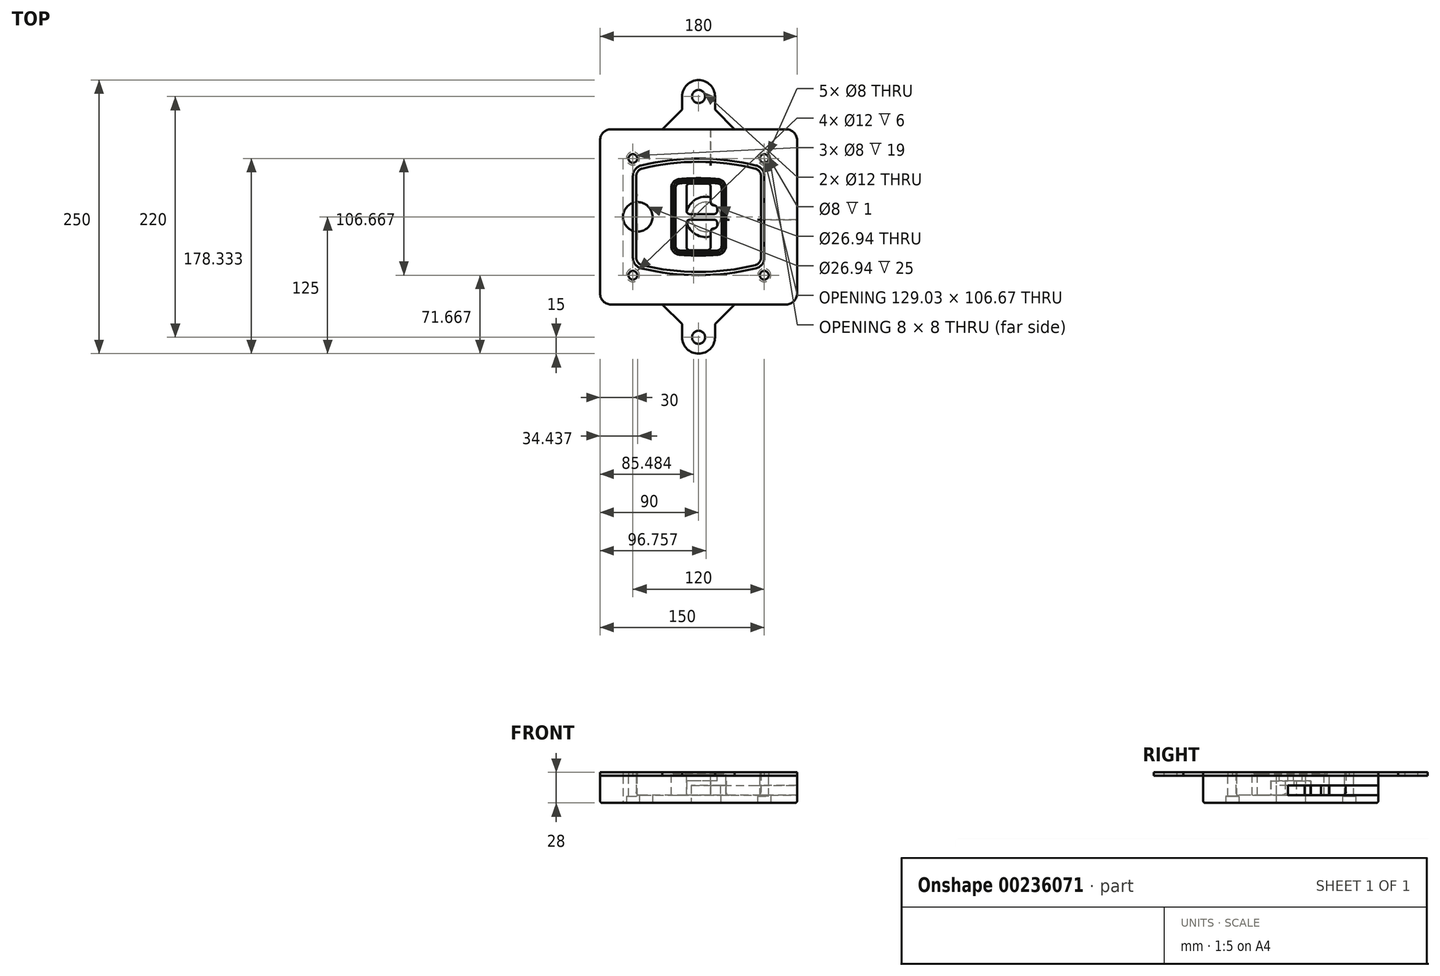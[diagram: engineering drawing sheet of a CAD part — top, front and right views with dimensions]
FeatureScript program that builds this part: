
annotation { "Feature Type Name" : "Feature", "Feature Type Description" : "" }
export const myFeature = defineFeature(function(context is Context, id is Id, definition is map)
    precondition{}
    {
        {
            var Q0;
            Q0=qCreatedBy(makeId("Top.planeOp"),FACE);
            var sketch = newSketch(context, id + "F0", { "sketchPlane" : qUnion([Q0])});
            skPoint(sketch, "E0.rect.middle", {"position": v(0, 0) * mm});
            skLineSegment(sketch, "E1.bottom", {"start": v(-80, -80) * mm, "end": v(80, -80) * mm});
            skLineSegment(sketch, "E1.top", {"start": v(-80, 80) * mm, "end": v(80, 80) * mm});
            skLineSegment(sketch, "E1.left", {"start": v(-90, -70) * mm, "end": v(-90, 70) * mm});
            skLineSegment(sketch, "E1.right", {"start": v(90, -70) * mm, "end": v(90, 70) * mm});
            skLineSegment(sketch, "E2", {"start": v(-90, 80) * mm, "end": v(90, -80) * mm, "construction": true});
            skLineSegment(sketch, "E3", {"start": v(90, 80) * mm, "end": v(-90, -80) * mm, "construction": true});
            skCircle(sketch, "E4", {"center": v(-60, 53.33) * mm, "radius": 4 * mm});
            skCircle(sketch, "E5", {"center": v(60, 53.33) * mm, "radius": 4 * mm});
            skCircle(sketch, "E6", {"center": v(60, -53.33) * mm, "radius": 4 * mm});
            skCircle(sketch, "E7", {"center": v(-60, -53.33) * mm, "radius": 4 * mm});
            skLineSegment(sketch, "E8", {"start": v(-60, 53.33) * mm, "end": v(60, 53.33) * mm, "construction": true});
            skLineSegment(sketch, "E9", {"start": v(60, 53.33) * mm, "end": v(60, -53.33) * mm, "construction": true});
            skLineSegment(sketch, "E10", {"start": v(60, -53.33) * mm, "end": v(-60, -53.33) * mm, "construction": true});
            skLineSegment(sketch, "E11", {"start": v(-60, -53.33) * mm, "end": v(-60, 53.33) * mm, "construction": true});
            skLineSegment(sketch, "E12", {"start": v(-60, 37.3) * mm, "end": v(-60, -37.3) * mm});
            skLineSegment(sketch, "E13", {"start": v(60, 37.3) * mm, "end": v(60, -37.3) * mm});
            skArc(sketch, "E14", {"start": v(52.38, 47.01) * mm, "mid": v(0, 53.33) * mm, "end": v(-52.38, 47.01) * mm});
            skArc(sketch, "E15", {"start": v(-52.38, -47.01) * mm, "mid": v(0, -53.33) * mm, "end": v(52.38, -47.01) * mm});
            skLineSegment(sketch, "E16", {"start": v(-60, 0) * mm, "end": v(60, 0) * mm, "construction": true});
            skPoint(sketch, "E17.visualSharp", {"position": v(-60, -45) * mm});
            skArc(sketch, "E17.filletArc", {"start": v(-60, -37.3) * mm, "mid": v(-57.87, -43.47) * mm, "end": v(-52.38, -47.01) * mm});
            skPoint(sketch, "E18.visualSharp", {"position": v(-60, 45) * mm});
            skArc(sketch, "E18.filletArc", {"start": v(-52.38, 47.01) * mm, "mid": v(-57.87, 43.47) * mm, "end": v(-60, 37.3) * mm});
            skPoint(sketch, "E19.visualSharp", {"position": v(60, 45) * mm});
            skArc(sketch, "E19.filletArc", {"start": v(60, 37.3) * mm, "mid": v(57.87, 43.47) * mm, "end": v(52.38, 47.01) * mm});
            skPoint(sketch, "E20.visualSharp", {"position": v(60, -45) * mm});
            skArc(sketch, "E20.filletArc", {"start": v(52.38, -47.01) * mm, "mid": v(57.87, -43.47) * mm, "end": v(60, -37.3) * mm});
            skPoint(sketch, "E21.visualSharp", {"position": v(-90, 80) * mm});
            skArc(sketch, "E21.filletArc", {"start": v(-80, 80) * mm, "mid": v(-87.07, 77.07) * mm, "end": v(-90, 70) * mm});
            skPoint(sketch, "E22.visualSharp", {"position": v(90, 80) * mm});
            skArc(sketch, "E22.filletArc", {"start": v(90, 70) * mm, "mid": v(87.07, 77.07) * mm, "end": v(80, 80) * mm});
            skPoint(sketch, "E23.visualSharp", {"position": v(90, -80) * mm});
            skArc(sketch, "E23.filletArc", {"start": v(80, -80) * mm, "mid": v(87.07, -77.07) * mm, "end": v(90, -70) * mm});
            skPoint(sketch, "E24.visualSharp", {"position": v(-90, -80) * mm});
            skArc(sketch, "E24.filletArc", {"start": v(-90, -70) * mm, "mid": v(-87.07, -77.07) * mm, "end": v(-80, -80) * mm});
            skArc(sketch, "E25.0", {"start": v(57, 37.3) * mm, "mid": v(55.5, 41.62) * mm, "end": v(51.67, 44.1) * mm});
            skLineSegment(sketch, "E25.1", {"start": v(57, 37.3) * mm, "end": v(57, -37.3) * mm});
            skArc(sketch, "E25.2", {"start": v(51.67, -44.1) * mm, "mid": v(55.5, -41.62) * mm, "end": v(57, -37.3) * mm});
            skArc(sketch, "E25.3", {"start": v(-51.67, -44.1) * mm, "mid": v(0, -50.33) * mm, "end": v(51.67, -44.1) * mm});
            skArc(sketch, "E25.4", {"start": v(-57, -37.3) * mm, "mid": v(-55.5, -41.62) * mm, "end": v(-51.67, -44.1) * mm});
            skArc(sketch, "E25.5", {"start": v(51.67, 44.1) * mm, "mid": v(0, 50.33) * mm, "end": v(-51.67, 44.1) * mm});
            skLineSegment(sketch, "E25.6", {"start": v(-57, 37.3) * mm, "end": v(-57, -37.3) * mm});
            skArc(sketch, "E25.7", {"start": v(-51.67, 44.1) * mm, "mid": v(-55.5, 41.62) * mm, "end": v(-57, 37.3) * mm});
            skArc(sketch, "E26.0", {"start": v(-53.33, 50.9) * mm, "mid": v(-61.01, 45.94) * mm, "end": v(-64, 37.3) * mm});
            skArc(sketch, "E26.1", {"start": v(53.33, 50.9) * mm, "mid": v(0, 57.33) * mm, "end": v(-53.33, 50.9) * mm});
            skArc(sketch, "E26.2", {"start": v(64, 37.3) * mm, "mid": v(61.01, 45.94) * mm, "end": v(53.33, 50.9) * mm});
            skLineSegment(sketch, "E26.3", {"start": v(64, 37.3) * mm, "end": v(64, -37.3) * mm});
            skArc(sketch, "E26.4", {"start": v(53.33, -50.9) * mm, "mid": v(61.01, -45.94) * mm, "end": v(64, -37.3) * mm});
            skLineSegment(sketch, "E26.5", {"start": v(-64, 37.3) * mm, "end": v(-64, -37.3) * mm});
            skArc(sketch, "E26.6", {"start": v(-53.33, -50.9) * mm, "mid": v(0, -57.33) * mm, "end": v(53.33, -50.9) * mm});
            skArc(sketch, "E26.7", {"start": v(-64, -37.3) * mm, "mid": v(-61.01, -45.94) * mm, "end": v(-53.33, -50.9) * mm});
            skSolve(sketch);
        }
        {
            var Q0;
            Q0=makeQuery(id+"F0.imprint","IMPRINT",FACE,{"disambiguationData":[TD([[makeQuery(id+"F0.imprint","IMPRINT",EDGE,{"derivedFrom":sQuery(id+"F0.wireOp",EDGE,"E1.bottom")}),1.0]])]});
            var Q1;
            Q1=makeQuery(id+"F0.imprint","IMPRINT",FACE,{"disambiguationData":[TD([[makeQuery(id+"F0.imprint","IMPRINT",EDGE,{"derivedFrom":sQuery(id+"F0.wireOp",EDGE,"E12")}),1.0]])]});
            var Q2;
            Q2=makeQuery(id+"F0.imprint","IMPRINT",FACE,{"disambiguationData":[TD([[makeQuery(id+"F0.imprint","IMPRINT",EDGE,{"derivedFrom":sQuery(id+"F0.wireOp",EDGE,"E25.0")}),1.0]])]});
            var Q3;
            Q3=makeQuery(id+"F0.imprint","IMPRINT",FACE,{"disambiguationData":[TD([[makeQuery(id+"F0.imprint","IMPRINT",EDGE,{"derivedFrom":sQuery(id+"F0.wireOp",EDGE,"E12")}),-1.0]])]});
            extrude(context, id + "F1", {"entities" : qUnion([Q0, Q1, Q2, Q3]), "oppositeDirection" : true, "depth" : 25 * mm});
        }
        {
            var Q0;
            Q0=makeQuery(id+"F0.imprint","IMPRINT",FACE,{"disambiguationData":[TD([[makeQuery(id+"F0.imprint","IMPRINT",EDGE,{"derivedFrom":sQuery(id+"F0.wireOp",EDGE,"E12")}),1.0]])]});
            extrude(context, id + "F2", {"entities" : qUnion([Q0]), "operationType" : NewBodyOperationType.ADD, "depth" : 3 * mm});
        }
        {
            var Q0;
            Q0=makeQuery(id+"F0.imprint","IMPRINT",FACE,{"disambiguationData":[TD([[makeQuery(id+"F0.imprint","IMPRINT",EDGE,{"derivedFrom":sQuery(id+"F0.wireOp",EDGE,"E25.0")}),1.0]])]});
            extrude(context, id + "F3", {"entities" : qUnion([Q0]), "operationType" : NewBodyOperationType.REMOVE, "oppositeDirection" : true, "depth" : 18 * mm});
        }
        {
            var Q0;
            Q0=makeQuery(id+"F2.opExtrude","CAP_FACE",FACE,{"disambiguationData":[OSD([sQuery(id+"F0.wireOp",EDGE,"E12"),sQuery(id+"F0.wireOp",EDGE,"E13"),sQuery(id+"F0.wireOp",EDGE,"E14"),sQuery(id+"F0.wireOp",EDGE,"E15"),sQuery(id+"F0.wireOp",EDGE,"E17.filletArc"),sQuery(id+"F0.wireOp",EDGE,"E18.filletArc"),sQuery(id+"F0.wireOp",EDGE,"E19.filletArc"),sQuery(id+"F0.wireOp",EDGE,"E20.filletArc"),sQuery(id+"F0.wireOp",EDGE,"E25.0"),sQuery(id+"F0.wireOp",EDGE,"E25.1"),sQuery(id+"F0.wireOp",EDGE,"E25.2"),sQuery(id+"F0.wireOp",EDGE,"E25.3"),sQuery(id+"F0.wireOp",EDGE,"E25.4"),sQuery(id+"F0.wireOp",EDGE,"E25.5"),sQuery(id+"F0.wireOp",EDGE,"E25.6"),sQuery(id+"F0.wireOp",EDGE,"E25.7")])],"isStart":false});
            var sketch = newSketch(context, id + "F4", { "sketchPlane" : qUnion([Q0])});
            skArc(sketch, "E27.0", {"start": v(-17.7, -34.56) * mm, "mid": v(0, -35.33) * mm, "end": v(17.7, -34.56) * mm});
            skArc(sketch, "E28.0", {"start": v(17.7, 34.56) * mm, "mid": v(0, 35.33) * mm, "end": v(-17.7, 34.56) * mm});
            skLineSegment(sketch, "E29", {"start": v(-25, 26.59) * mm, "end": v(-25, -26.59) * mm});
            skLineSegment(sketch, "E30", {"start": v(25, 26.59) * mm, "end": v(25, -26.59) * mm});
            skLineSegment(sketch, "E31", {"start": v(-25, 33.78) * mm, "end": v(25, 33.78) * mm, "construction": true});
            skLineSegment(sketch, "E32", {"start": v(-25, -33.78) * mm, "end": v(25, -33.78) * mm, "construction": true});
            skPoint(sketch, "E33.visualSharp", {"position": v(-25, 33.78) * mm});
            skArc(sketch, "E33.filletArc", {"start": v(-17.7, 34.56) * mm, "mid": v(-22.9, 32) * mm, "end": v(-25, 26.59) * mm});
            skPoint(sketch, "E34.visualSharp", {"position": v(25, 33.78) * mm});
            skArc(sketch, "E34.filletArc", {"start": v(25, 26.59) * mm, "mid": v(22.9, 32) * mm, "end": v(17.7, 34.56) * mm});
            skPoint(sketch, "E35.visualSharp", {"position": v(25, -33.78) * mm});
            skArc(sketch, "E35.filletArc", {"start": v(17.7, -34.56) * mm, "mid": v(22.9, -32) * mm, "end": v(25, -26.59) * mm});
            skPoint(sketch, "E36.visualSharp", {"position": v(-25, -33.78) * mm});
            skArc(sketch, "E36.filletArc", {"start": v(-25, -26.59) * mm, "mid": v(-22.9, -32) * mm, "end": v(-17.7, -34.56) * mm});
            skArc(sketch, "E37.0", {"start": v(51.67, 44.1) * mm, "mid": v(0, 50.33) * mm, "end": v(-51.67, 44.1) * mm});
            skArc(sketch, "E37.1", {"start": v(-51.67, 44.1) * mm, "mid": v(-55.5, 41.62) * mm, "end": v(-57, 37.3) * mm});
            skLineSegment(sketch, "E37.2", {"start": v(-57, 37.3) * mm, "end": v(-57, -37.3) * mm});
            skArc(sketch, "E37.3", {"start": v(-57, -37.3) * mm, "mid": v(-55.5, -41.62) * mm, "end": v(-51.67, -44.1) * mm});
            skArc(sketch, "E37.4", {"start": v(-51.67, -44.1) * mm, "mid": v(0, -50.33) * mm, "end": v(51.67, -44.1) * mm});
            skArc(sketch, "E37.5", {"start": v(51.67, -44.1) * mm, "mid": v(55.5, -41.62) * mm, "end": v(57, -37.3) * mm});
            skLineSegment(sketch, "E37.6", {"start": v(57, 37.3) * mm, "end": v(57, -37.3) * mm});
            skArc(sketch, "E37.7", {"start": v(57, 37.3) * mm, "mid": v(55.5, 41.62) * mm, "end": v(51.67, 44.1) * mm});
            skLineSegment(sketch, "E38.0", {"start": v(23, 26.59) * mm, "end": v(23, -26.59) * mm});
            skArc(sketch, "E38.1", {"start": v(17.53, -32.56) * mm, "mid": v(21.42, -30.64) * mm, "end": v(23, -26.59) * mm});
            skArc(sketch, "E38.2", {"start": v(-17.53, -32.56) * mm, "mid": v(0, -33.33) * mm, "end": v(17.53, -32.56) * mm});
            skArc(sketch, "E38.3", {"start": v(-23, -26.59) * mm, "mid": v(-21.42, -30.64) * mm, "end": v(-17.53, -32.56) * mm});
            skLineSegment(sketch, "E38.4", {"start": v(-23, 26.59) * mm, "end": v(-23, -26.59) * mm});
            skArc(sketch, "E38.5", {"start": v(23, 26.59) * mm, "mid": v(21.42, 30.64) * mm, "end": v(17.53, 32.56) * mm});
            skArc(sketch, "E38.6", {"start": v(-17.53, 32.56) * mm, "mid": v(-21.42, 30.64) * mm, "end": v(-23, 26.59) * mm});
            skArc(sketch, "E38.7", {"start": v(17.53, 32.56) * mm, "mid": v(0, 33.33) * mm, "end": v(-17.53, 32.56) * mm});
            skArc(sketch, "E39.0", {"start": v(21, 26.59) * mm, "mid": v(19.95, 29.29) * mm, "end": v(17.35, 30.57) * mm});
            skLineSegment(sketch, "E39.1", {"start": v(21, 26.59) * mm, "end": v(21, -26.59) * mm});
            skArc(sketch, "E39.2", {"start": v(17.35, -30.57) * mm, "mid": v(19.95, -29.29) * mm, "end": v(21, -26.59) * mm});
            skArc(sketch, "E39.3", {"start": v(-17.35, -30.57) * mm, "mid": v(0, -31.33) * mm, "end": v(17.35, -30.57) * mm});
            skArc(sketch, "E39.4", {"start": v(-21, -26.59) * mm, "mid": v(-19.95, -29.29) * mm, "end": v(-17.35, -30.57) * mm});
            skArc(sketch, "E39.5", {"start": v(17.35, 30.57) * mm, "mid": v(0, 31.33) * mm, "end": v(-17.35, 30.57) * mm});
            skLineSegment(sketch, "E39.6", {"start": v(-21, 26.59) * mm, "end": v(-21, -26.59) * mm});
            skArc(sketch, "E39.7", {"start": v(-17.35, 30.57) * mm, "mid": v(-19.95, 29.29) * mm, "end": v(-21, 26.59) * mm});
            skLineSegment(sketch, "E40", {"start": v(-25, 0) * mm, "end": v(25, 0) * mm, "construction": true});
            skLineSegment(sketch, "E41", {"start": v(-11, 5.5) * mm, "end": v(-11, 27.5) * mm});
            skLineSegment(sketch, "E42", {"start": v(-8, 30.5) * mm, "end": v(8, 30.5) * mm});
            skLineSegment(sketch, "E43", {"start": v(11, 27.5) * mm, "end": v(11, 13.5) * mm});
            skLineSegment(sketch, "E44", {"start": v(14, 10.5) * mm, "end": v(14, 10.5) * mm});
            skLineSegment(sketch, "E45", {"start": v(17, 7.5) * mm, "end": v(17, 5.5) * mm});
            skLineSegment(sketch, "E46", {"start": v(14, 2.5) * mm, "end": v(-8, 2.5) * mm});
            skPoint(sketch, "E47.visualSharp", {"position": v(-11, 30.5) * mm});
            skArc(sketch, "E47.filletArc", {"start": v(-8, 30.5) * mm, "mid": v(-10.12, 29.62) * mm, "end": v(-11, 27.5) * mm});
            skPoint(sketch, "E48.visualSharp", {"position": v(11, 30.5) * mm});
            skArc(sketch, "E48.filletArc", {"start": v(11, 27.5) * mm, "mid": v(10.12, 29.62) * mm, "end": v(8, 30.5) * mm});
            skPoint(sketch, "E49.visualSharp", {"position": v(11, 10.5) * mm});
            skArc(sketch, "E49.filletArc", {"start": v(11, 13.5) * mm, "mid": v(11.88, 11.38) * mm, "end": v(14, 10.5) * mm});
            skPoint(sketch, "E50.visualSharp", {"position": v(17, 10.5) * mm});
            skArc(sketch, "E50.filletArc", {"start": v(17, 7.5) * mm, "mid": v(16.12, 9.62) * mm, "end": v(14, 10.5) * mm});
            skPoint(sketch, "E51.visualSharp", {"position": v(17, 2.5) * mm});
            skArc(sketch, "E51.filletArc", {"start": v(14, 2.5) * mm, "mid": v(16.12, 3.38) * mm, "end": v(17, 5.5) * mm});
            skPoint(sketch, "E52.visualSharp", {"position": v(-11, 2.5) * mm});
            skArc(sketch, "E52.filletArc", {"start": v(-11, 5.5) * mm, "mid": v(-10.12, 3.38) * mm, "end": v(-8, 2.5) * mm});
            skLineSegment(sketch, "E53.0.MirrorCS", {"start": v(14, -2.5) * mm, "end": v(-8, -2.5) * mm});
            skArc(sketch, "E54.0.MirrorCS", {"start": v(-11, -5.5) * mm, "mid": v(-10.12, -3.38) * mm, "end": v(-8, -2.5) * mm});
            skLineSegment(sketch, "E55.0.MirrorCS", {"start": v(-11, -5.5) * mm, "end": v(-11, -27.5) * mm});
            skArc(sketch, "E56.0.MirrorCS", {"start": v(-8, -30.5) * mm, "mid": v(-10.12, -29.62) * mm, "end": v(-11, -27.5) * mm});
            skLineSegment(sketch, "E57.0.MirrorCS", {"start": v(-8, -30.5) * mm, "end": v(8, -30.5) * mm});
            skArc(sketch, "E58.0.MirrorCS", {"start": v(11, -27.5) * mm, "mid": v(10.12, -29.62) * mm, "end": v(8, -30.5) * mm});
            skLineSegment(sketch, "E59.0.MirrorCS", {"start": v(11, -27.5) * mm, "end": v(11, -13.5) * mm});
            skArc(sketch, "E60.0.MirrorCS", {"start": v(11, -13.5) * mm, "mid": v(11.88, -11.38) * mm, "end": v(14, -10.5) * mm});
            skArc(sketch, "E61.0.MirrorCS", {"start": v(17, -7.5) * mm, "mid": v(16.12, -9.62) * mm, "end": v(14, -10.5) * mm});
            skLineSegment(sketch, "E62.0.MirrorCS", {"start": v(17, -7.5) * mm, "end": v(17, -5.5) * mm});
            skArc(sketch, "E63.0.MirrorCS", {"start": v(14, -2.5) * mm, "mid": v(16.12, -3.38) * mm, "end": v(17, -5.5) * mm});
            skSolve(sketch);
        }
        {
            var Q0;
            Q0=makeQuery(id+"F4.imprint","IMPRINT",FACE,{"disambiguationData":[TD([[makeQuery(id+"F4.imprint","IMPRINT",EDGE,{"derivedFrom":sQuery(id+"F4.wireOp",EDGE,"E27.0")}),1.0]])]});
            var Q1;
            Q1=makeQuery(id+"F4.imprint","IMPRINT",FACE,{"disambiguationData":[TD([[makeQuery(id+"F4.imprint","IMPRINT",EDGE,{"derivedFrom":sQuery(id+"F4.wireOp",EDGE,"E38.0")}),-1.0]])]});
            var Q2;
            Q2=makeQuery(id+"F4.imprint","IMPRINT",FACE,{"disambiguationData":[TD([[makeQuery(id+"F4.imprint","IMPRINT",EDGE,{"derivedFrom":sQuery(id+"F4.wireOp",EDGE,"E39.0")}),1.0]])]});
            extrude(context, id + "F5", {"entities" : qUnion([Q0, Q1, Q2]), "operationType" : NewBodyOperationType.ADD, "endBound" : BoundingType.UP_TO_NEXT, "oppositeDirection" : true, "depth" : 25 * mm});
        }
        {
            var Q0;
            Q0=makeQuery(id+"F4.imprint","IMPRINT",FACE,{"disambiguationData":[TD([[makeQuery(id+"F4.imprint","IMPRINT",EDGE,{"derivedFrom":sQuery(id+"F4.wireOp",EDGE,"E38.0")}),-1.0]])]});
            extrude(context, id + "F6", {"entities" : qUnion([Q0]), "operationType" : NewBodyOperationType.REMOVE, "oppositeDirection" : true, "depth" : 2 * mm});
        }
        {
            var Q0;
            Q0=makeQuery(id+"F1.opExtrude","CAP_FACE",FACE,{"disambiguationData":[OSD([sQuery(id+"F0.wireOp",EDGE,"E1.bottom"),sQuery(id+"F0.wireOp",EDGE,"E1.top"),sQuery(id+"F0.wireOp",EDGE,"E1.left"),sQuery(id+"F0.wireOp",EDGE,"E1.right"),sQuery(id+"F0.wireOp",EDGE,"E4"),sQuery(id+"F0.wireOp",EDGE,"E5"),sQuery(id+"F0.wireOp",EDGE,"E6"),sQuery(id+"F0.wireOp",EDGE,"E7"),sQuery(id+"F0.wireOp",EDGE,"E21.filletArc"),sQuery(id+"F0.wireOp",EDGE,"E22.filletArc"),sQuery(id+"F0.wireOp",EDGE,"E23.filletArc"),sQuery(id+"F0.wireOp",EDGE,"E24.filletArc")])],"isStart":false});
            var sketch = newSketch(context, id + "F7", { "sketchPlane" : qUnion([Q0])});
            skCircle(sketch, "E64", {"center": v(6.76, 0) * mm, "radius": 13.47 * mm});
            skCircle(sketch, "E65", {"center": v(-55.56, 0) * mm, "radius": 13.47 * mm});
            skLineSegment(sketch, "E66", {"start": v(90, 0) * mm, "end": v(-90, 0) * mm});
            skCircle(sketch, "E67", {"center": v(6.76, 0) * mm, "radius": 18.47 * mm});
            skCircle(sketch, "E68", {"center": v(60, -53.33) * mm, "radius": 6 * mm});
            skCircle(sketch, "E69", {"center": v(-60, -53.33) * mm, "radius": 6 * mm});
            skCircle(sketch, "E70", {"center": v(-60, 53.33) * mm, "radius": 6 * mm});
            skCircle(sketch, "E71", {"center": v(60, 53.33) * mm, "radius": 6 * mm});
            skSolve(sketch);
        }
        {
            var Q0;
            {var subQ1=sQuery(id+"F7.wireOp",EDGE,"E66");var subQ4=sQuery(id+"F7.wireOp",EDGE,"E64");var subQ6=makeQuery(id+"F7.imprint","INTERSECT",VERTEX,{"disambiguationData":[OD(0.0)],"derivedFrom":[subQ4,subQ1]});Q0=makeQuery(id+"F7.imprint","IMPRINT",FACE,{"disambiguationData":[TD([[makeQuery(id+"F7.imprint","IMPRINT",EDGE,{"disambiguationData":[TD([[subQ6,-1.0]])],"derivedFrom":subQ4}),-1.0]])]});}
            var Q1;
            {var subQ0=sQuery(id+"F7.wireOp",EDGE,"E66");var subQ1=sQuery(id+"F7.wireOp",EDGE,"E64");var subQ3=makeQuery(id+"F7.imprint","INTERSECT",VERTEX,{"disambiguationData":[OD(0.0)],"derivedFrom":[subQ1,subQ0]});Q1=makeQuery(id+"F7.imprint","IMPRINT",FACE,{"disambiguationData":[TD([[makeQuery(id+"F7.imprint","IMPRINT",EDGE,{"disambiguationData":[TD([[subQ3,-1.0]])],"derivedFrom":subQ1}),1.0]])]});}
            var Q2;
            {var subQ0=sQuery(id+"F7.wireOp",EDGE,"E66");var subQ1=sQuery(id+"F7.wireOp",EDGE,"E64");var subQ3=makeQuery(id+"F7.imprint","INTERSECT",VERTEX,{"disambiguationData":[OD(0.0)],"derivedFrom":[subQ1,subQ0]});Q2=makeQuery(id+"F7.imprint","IMPRINT",FACE,{"disambiguationData":[TD([[makeQuery(id+"F7.imprint","IMPRINT",EDGE,{"disambiguationData":[TD([[subQ3,1.0]])],"derivedFrom":subQ1}),1.0]])]});}
            var Q3;
            {var subQ1=sQuery(id+"F7.wireOp",EDGE,"E66");var subQ4=sQuery(id+"F7.wireOp",EDGE,"E64");var subQ6=makeQuery(id+"F7.imprint","INTERSECT",VERTEX,{"disambiguationData":[OD(0.0)],"derivedFrom":[subQ4,subQ1]});Q3=makeQuery(id+"F7.imprint","IMPRINT",FACE,{"disambiguationData":[TD([[makeQuery(id+"F7.imprint","IMPRINT",EDGE,{"disambiguationData":[TD([[subQ6,1.0]])],"derivedFrom":subQ4}),-1.0]])]});}
            extrude(context, id + "F8", {"entities" : qUnion([Q0, Q1, Q2, Q3]), "operationType" : NewBodyOperationType.ADD, "oppositeDirection" : true, "depth" : 20 * mm});
        }
        {
            var Q0;
            {var subQ0=sQuery(id+"F7.wireOp",EDGE,"E66");var subQ1=sQuery(id+"F7.wireOp",EDGE,"E64");var subQ3=makeQuery(id+"F7.imprint","INTERSECT",VERTEX,{"disambiguationData":[OD(0.0)],"derivedFrom":[subQ1,subQ0]});Q0=makeQuery(id+"F7.imprint","IMPRINT",FACE,{"disambiguationData":[TD([[makeQuery(id+"F7.imprint","IMPRINT",EDGE,{"disambiguationData":[TD([[subQ3,-1.0]])],"derivedFrom":subQ1}),1.0]])]});}
            var Q1;
            {var subQ0=sQuery(id+"F7.wireOp",EDGE,"E66");var subQ1=sQuery(id+"F7.wireOp",EDGE,"E64");var subQ3=makeQuery(id+"F7.imprint","INTERSECT",VERTEX,{"disambiguationData":[OD(0.0)],"derivedFrom":[subQ1,subQ0]});Q1=makeQuery(id+"F7.imprint","IMPRINT",FACE,{"disambiguationData":[TD([[makeQuery(id+"F7.imprint","IMPRINT",EDGE,{"disambiguationData":[TD([[subQ3,1.0]])],"derivedFrom":subQ1}),1.0]])]});}
            extrude(context, id + "F9", {"entities" : qUnion([Q0, Q1]), "operationType" : NewBodyOperationType.REMOVE, "oppositeDirection" : true, "depth" : 16 * mm});
        }
        {
            var Q0;
            {var subQ0=sQuery(id+"F7.wireOp",EDGE,"E66");var subQ1=sQuery(id+"F7.wireOp",EDGE,"E65");var subQ3=makeQuery(id+"F7.imprint","INTERSECT",VERTEX,{"disambiguationData":[OD(0.0)],"derivedFrom":[subQ1,subQ0]});Q0=makeQuery(id+"F7.imprint","IMPRINT",FACE,{"disambiguationData":[TD([[makeQuery(id+"F7.imprint","IMPRINT",EDGE,{"disambiguationData":[TD([[subQ3,-1.0]])],"derivedFrom":subQ1}),1.0]])]});}
            var Q1;
            {var subQ0=sQuery(id+"F7.wireOp",EDGE,"E66");var subQ1=sQuery(id+"F7.wireOp",EDGE,"E65");var subQ3=makeQuery(id+"F7.imprint","INTERSECT",VERTEX,{"disambiguationData":[OD(0.0)],"derivedFrom":[subQ1,subQ0]});Q1=makeQuery(id+"F7.imprint","IMPRINT",FACE,{"disambiguationData":[TD([[makeQuery(id+"F7.imprint","IMPRINT",EDGE,{"disambiguationData":[TD([[subQ3,1.0]])],"derivedFrom":subQ1}),1.0]])]});}
            extrude(context, id + "F10", {"entities" : qUnion([Q0, Q1]), "operationType" : NewBodyOperationType.REMOVE, "oppositeDirection" : true, "depth" : 25 * mm});
        }
        {
            var Q0;
            Q0=makeQuery(id+"F7.imprint","IMPRINT",FACE,{"disambiguationData":[TD([[makeQuery(id+"F7.imprint","IMPRINT",EDGE,{"derivedFrom":sQuery(id+"F7.wireOp",EDGE,"E68")}),1.0]])]});
            var Q1;
            Q1=makeQuery(id+"F7.imprint","IMPRINT",FACE,{"disambiguationData":[TD([[makeQuery(id+"F7.imprint","IMPRINT",EDGE,{"derivedFrom":makeQuery(id+"F1.opExtrude","CAP_EDGE",EDGE,{"disambiguationData":[OSD([sQuery(id+"F0.wireOp",EDGE,"E5")])],"isStart":false})}),-1.0]])]});
            var Q2;
            Q2=makeQuery(id+"F7.imprint","IMPRINT",FACE,{"disambiguationData":[TD([[makeQuery(id+"F7.imprint","IMPRINT",EDGE,{"derivedFrom":sQuery(id+"F7.wireOp",EDGE,"E69")}),1.0]])]});
            var Q3;
            Q3=makeQuery(id+"F7.imprint","IMPRINT",FACE,{"disambiguationData":[TD([[makeQuery(id+"F7.imprint","IMPRINT",EDGE,{"derivedFrom":makeQuery(id+"F1.opExtrude","CAP_EDGE",EDGE,{"disambiguationData":[OSD([sQuery(id+"F0.wireOp",EDGE,"E4")])],"isStart":false})}),-1.0]])]});
            var Q4;
            Q4=makeQuery(id+"F7.imprint","IMPRINT",FACE,{"disambiguationData":[TD([[makeQuery(id+"F7.imprint","IMPRINT",EDGE,{"derivedFrom":sQuery(id+"F7.wireOp",EDGE,"E70")}),1.0]])]});
            var Q5;
            Q5=makeQuery(id+"F7.imprint","IMPRINT",FACE,{"disambiguationData":[TD([[makeQuery(id+"F7.imprint","IMPRINT",EDGE,{"derivedFrom":makeQuery(id+"F1.opExtrude","CAP_EDGE",EDGE,{"disambiguationData":[OSD([sQuery(id+"F0.wireOp",EDGE,"E7")])],"isStart":false})}),-1.0]])]});
            var Q6;
            Q6=makeQuery(id+"F7.imprint","IMPRINT",FACE,{"disambiguationData":[TD([[makeQuery(id+"F7.imprint","IMPRINT",EDGE,{"derivedFrom":sQuery(id+"F7.wireOp",EDGE,"E71")}),1.0]])]});
            var Q7;
            Q7=makeQuery(id+"F7.imprint","IMPRINT",FACE,{"disambiguationData":[TD([[makeQuery(id+"F7.imprint","IMPRINT",EDGE,{"derivedFrom":makeQuery(id+"F1.opExtrude","CAP_EDGE",EDGE,{"disambiguationData":[OSD([sQuery(id+"F0.wireOp",EDGE,"E6")])],"isStart":false})}),-1.0]])]});
            extrude(context, id + "F11", {"entities" : qUnion([Q0, Q1, Q2, Q3, Q4, Q5, Q6, Q7]), "operationType" : NewBodyOperationType.REMOVE, "oppositeDirection" : true, "depth" : 6 * mm});
        }
        {
            var Q0;
            Q0=makeQuery(id+"F9.boolean.opBoolean","COPY",FACE,{"derivedFrom":makeQuery(id+"F9.opExtrude","CAP_FACE",FACE,{"disambiguationData":[OSD([sQuery(id+"F7.wireOp",EDGE,"E64")])],"isStart":false})});
            var sketch = newSketch(context, id + "F12", { "sketchPlane" : qUnion([Q0])});
            skArc(sketch, "E72.0", {"start": v(11, -88.19) * mm, "mid": v(97.1, -83.6) * mm, "end": v(92.5, 2.5) * mm});
            skLineSegment(sketch, "E72.1", {"start": v(11, -17.97) * mm, "end": v(11, -17.97) * mm});
            skLineSegment(sketch, "E73", {"start": v(92.5, -105.13) * mm, "end": v(102.3, -105.13) * mm});
            skLineSegment(sketch, "E74.0", {"start": v(92.5, 2.5) * mm, "end": v(14, 2.5) * mm});
            skArc(sketch, "E74.1", {"start": v(14, 2.5) * mm, "mid": v(16.12, 3.38) * mm, "end": v(17, 5.5) * mm});
            skLineSegment(sketch, "E74.2", {"start": v(17, 7.5) * mm, "end": v(17, 5.5) * mm});
            skArc(sketch, "E74.3", {"start": v(17, 7.5) * mm, "mid": v(16.12, 9.62) * mm, "end": v(14, 10.5) * mm});
            skArc(sketch, "E74.4", {"start": v(11, 13.5) * mm, "mid": v(11.88, 11.38) * mm, "end": v(14, 10.5) * mm});
            skLineSegment(sketch, "E74.5", {"start": v(11, 13.5) * mm, "end": v(11, -88.19) * mm});
            skLineSegment(sketch, "E74.7", {"start": v(92.5, -2.5) * mm, "end": v(14, -2.5) * mm});
            skArc(sketch, "E74.8", {"start": v(14, -2.5) * mm, "mid": v(16.12, -3.38) * mm, "end": v(17, -5.5) * mm});
            skLineSegment(sketch, "E74.9", {"start": v(17, -7.5) * mm, "end": v(17, -5.5) * mm});
            skArc(sketch, "E74.10", {"start": v(17, -7.5) * mm, "mid": v(16.12, -9.62) * mm, "end": v(14, -10.5) * mm});
            skArc(sketch, "E74.11", {"start": v(11, -13.5) * mm, "mid": v(11.88, -11.38) * mm, "end": v(14, -10.5) * mm});
            skLineSegment(sketch, "E74.12", {"start": v(11, -17.97) * mm, "end": v(11, -13.5) * mm});
            skPoint(sketch, "E75.orphan", {"position": v(11, -27.5) * mm});
            skPoint(sketch, "E76.orphan", {"position": v(-8, -2.5) * mm});
            skPoint(sketch, "E77.orphan", {"position": v(-8, 2.5) * mm});
            skPoint(sketch, "E78.orphan", {"position": v(11, 27.5) * mm});
            skSolve(sketch);
        }
        {
            var Q0;
            {var subQ7=sQuery(id+"F12.wireOp",EDGE,"E72.0");var subQ14=sQuery(id+"F12.wireOp",EDGE,"E72.1");var subQ16=sQuery(id+"F12.wireOp",EDGE,"E74.1");var subQ18=sQuery(id+"F12.wireOp",EDGE,"E74.8");Q0=qUnion([makeQuery(id+"F12.imprint","IMPRINT",FACE,{"disambiguationData":[TD([[makeQuery(id+"F12.imprint","IMPRINT",EDGE,{"derivedFrom":subQ7}),1.0]])]}),makeQuery(id+"F12.imprint","IMPRINT",FACE,{"disambiguationData":[TD([[makeQuery(id+"F12.imprint","IMPRINT",EDGE,{"derivedFrom":subQ14}),1.0]])]}),makeQuery(id+"F12.imprint","IMPRINT",FACE,{"disambiguationData":[TD([[makeQuery(id+"F12.imprint","IMPRINT",EDGE,{"derivedFrom":subQ16}),1.0]])]}),makeQuery(id+"F12.imprint","IMPRINT",FACE,{"disambiguationData":[TD([[makeQuery(id+"F12.imprint","IMPRINT",EDGE,{"derivedFrom":subQ18}),-1.0]])]})]);}
            var Q1;
            Q1=makeQuery(id+"F5.boolean.opBoolean","SPLIT",FACE,{"disambiguationData":[TD([makeQuery(id+"F5.opExtrude","SWEPT_FACE",FACE,{"disambiguationData":[OSD([sQuery(id+"F4.wireOp",EDGE,"E41")])]})])],"derivedFrom":makeQuery(id+"F3.boolean.opBoolean","COPY",FACE,{"derivedFrom":makeQuery(id+"F3.opExtrude","CAP_FACE",FACE,{"disambiguationData":[OSD([sQuery(id+"F0.wireOp",EDGE,"E25.0"),sQuery(id+"F0.wireOp",EDGE,"E25.1"),sQuery(id+"F0.wireOp",EDGE,"E25.2"),sQuery(id+"F0.wireOp",EDGE,"E25.3"),sQuery(id+"F0.wireOp",EDGE,"E25.4"),sQuery(id+"F0.wireOp",EDGE,"E25.5"),sQuery(id+"F0.wireOp",EDGE,"E25.6"),sQuery(id+"F0.wireOp",EDGE,"E25.7")])],"isStart":false})})});
            extrude(context, id + "F13", {"entities" : qUnion([Q0]), "operationType" : NewBodyOperationType.REMOVE, "endBound" : BoundingType.UP_TO_SURFACE, "endBoundEntityFace" : qUnion([Q1]), "depth" : 25 * mm});
        }
        {
            var Q0;
            Q0=makeQuery(id+"F3.boolean.opBoolean","COPY",EDGE,{"derivedFrom":makeQuery(id+"F3.opExtrude","CAP_EDGE",EDGE,{"disambiguationData":[OSD([sQuery(id+"F0.wireOp",EDGE,"E25.6")])],"isStart":false})});
            var Q1;
            Q1=makeQuery(id+"F8.boolean.opBoolean","INTERSECT",EDGE,{"derivedFrom":[makeQuery(id+"F5.opExtrude","SWEPT_FACE",FACE,{"disambiguationData":[OSD([sQuery(id+"F4.wireOp",EDGE,"E30")])]}),makeQuery(id+"F8.opExtrude","CAP_FACE",FACE,{"disambiguationData":[OSD([sQuery(id+"F7.wireOp",EDGE,"E67")])],"isStart":false})]});
            var Q2;
            Q2=makeQuery(id+"F8.boolean.opBoolean","INTERSECT",EDGE,{"disambiguationData":[OD(1.0)],"derivedFrom":[makeQuery(id+"F5.opExtrude","SWEPT_FACE",FACE,{"disambiguationData":[OSD([sQuery(id+"F4.wireOp",EDGE,"E30")])]}),makeQuery(id+"F8.opExtrude","SWEPT_FACE",FACE,{"disambiguationData":[OSD([sQuery(id+"F7.wireOp",EDGE,"E67")])]})]});
            var Q3;
            {var subQ0=makeQuery(id+"F3.boolean.opBoolean","COPY",FACE,{"derivedFrom":makeQuery(id+"F3.opExtrude","CAP_FACE",FACE,{"disambiguationData":[OSD([sQuery(id+"F0.wireOp",EDGE,"E25.0"),sQuery(id+"F0.wireOp",EDGE,"E25.1"),sQuery(id+"F0.wireOp",EDGE,"E25.2"),sQuery(id+"F0.wireOp",EDGE,"E25.3"),sQuery(id+"F0.wireOp",EDGE,"E25.4"),sQuery(id+"F0.wireOp",EDGE,"E25.5"),sQuery(id+"F0.wireOp",EDGE,"E25.6"),sQuery(id+"F0.wireOp",EDGE,"E25.7")])],"isStart":false})});var subQ1=sQuery(id+"F4.wireOp",EDGE,"E30");Q3=makeQuery(id+"F8.boolean.opBoolean","SPLIT",EDGE,{"disambiguationData":[TD([makeQuery(id+"F5.opExtrude","SWEPT_FACE",FACE,{"disambiguationData":[OSD([sQuery(id+"F4.wireOp",EDGE,"E35.filletArc")])]})])],"derivedFrom":makeQuery(id+"F5.opExtrude","TWEAK_EDGE",EDGE,{"derivedFrom":[subQ0,makeQuery(id+"F4.imprint","IMPRINT",EDGE,{"derivedFrom":subQ1})]})});}
            var Q4;
            {var subQ0=sQuery(id+"F0.wireOp",EDGE,"E25.0");var subQ1=sQuery(id+"F0.wireOp",EDGE,"E25.1");var subQ2=sQuery(id+"F0.wireOp",EDGE,"E25.2");var subQ3=sQuery(id+"F0.wireOp",EDGE,"E25.3");var subQ4=sQuery(id+"F0.wireOp",EDGE,"E25.4");var subQ5=sQuery(id+"F0.wireOp",EDGE,"E25.5");var subQ6=sQuery(id+"F0.wireOp",EDGE,"E25.6");var subQ7=sQuery(id+"F0.wireOp",EDGE,"E25.7");Q4=makeQuery(id+"F8.boolean.opBoolean","INTERSECT",EDGE,{"derivedFrom":[makeQuery(id+"F5.boolean.opBoolean","SPLIT",FACE,{"disambiguationData":[TD([makeQuery(id+"F2.opExtrude","SWEPT_FACE",FACE,{"disambiguationData":[OSD([subQ0])]})])],"derivedFrom":makeQuery(id+"F3.boolean.opBoolean","COPY",FACE,{"derivedFrom":makeQuery(id+"F3.opExtrude","CAP_FACE",FACE,{"disambiguationData":[OSD([subQ0,subQ1,subQ2,subQ3,subQ4,subQ5,subQ6,subQ7])],"isStart":false})})}),makeQuery(id+"F8.opExtrude","SWEPT_FACE",FACE,{"disambiguationData":[OSD([sQuery(id+"F7.wireOp",EDGE,"E67")])]})]});}
            var Q5;
            Q5=makeQuery(id+"F8.boolean.opBoolean","INTERSECT",EDGE,{"disambiguationData":[OD(0.0)],"derivedFrom":[makeQuery(id+"F5.opExtrude","SWEPT_FACE",FACE,{"disambiguationData":[OSD([sQuery(id+"F4.wireOp",EDGE,"E30")])]}),makeQuery(id+"F8.opExtrude","SWEPT_FACE",FACE,{"disambiguationData":[OSD([sQuery(id+"F7.wireOp",EDGE,"E67")])]})]});
            fillet(context, id + "F14", {"entities" : qUnion([Q0, Q1, Q2, Q3, Q4, Q5]), "radius" : 3 * mm, "tangentPropagation" : true, "allowEdgeOverflow" : false});
        }
        {
            var Q0;
            Q0=makeQuery(id+"F1.opExtrude","CAP_EDGE",EDGE,{"disambiguationData":[OSD([sQuery(id+"F0.wireOp",EDGE,"E1.bottom")])],"isStart":false});
            fillet(context, id + "F15", {"entities" : qUnion([Q0]), "radius" : 2 * mm, "tangentPropagation" : true, "allowEdgeOverflow" : false});
        }
        {
            var Q0;
            {var subQ0=sQuery(id+"F0.wireOp",EDGE,"E22.filletArc");var subQ1=sQuery(id+"F0.wireOp",EDGE,"E7");var subQ2=sQuery(id+"F0.wireOp",EDGE,"E6");var subQ3=sQuery(id+"F0.wireOp",EDGE,"E5");var subQ4=sQuery(id+"F0.wireOp",EDGE,"E4");var subQ5=sQuery(id+"F0.wireOp",EDGE,"E1.bottom");var subQ6=sQuery(id+"F0.wireOp",EDGE,"E21.filletArc");var subQ7=sQuery(id+"F0.wireOp",EDGE,"E1.top");var subQ8=sQuery(id+"F0.wireOp",EDGE,"E1.left");var subQ9=sQuery(id+"F0.wireOp",EDGE,"E1.right");var subQ10=sQuery(id+"F0.wireOp",EDGE,"E23.filletArc");var subQ11=sQuery(id+"F0.wireOp",EDGE,"E24.filletArc");Q0=makeQuery(id+"F2.boolean.opBoolean","SPLIT",FACE,{"disambiguationData":[TD([makeQuery(id+"F1.opExtrude","SWEPT_FACE",FACE,{"disambiguationData":[OSD([subQ5])]})])],"derivedFrom":makeQuery(id+"F1.opExtrude","CAP_FACE",FACE,{"disambiguationData":[OSD([subQ5,subQ7,subQ8,subQ9,subQ4,subQ3,subQ2,subQ1,subQ6,subQ0,subQ10,subQ11])],"isStart":true})});}
            var sketch = newSketch(context, id + "F16", { "sketchPlane" : qUnion([Q0])});
            skArc(sketch, "E79.0", {"start": v(-80, 80) * mm, "mid": v(-87.07, 77.07) * mm, "end": v(-90, 70) * mm});
            skLineSegment(sketch, "E79.1", {"start": v(-80, 80) * mm, "end": v(80, 80) * mm});
            skArc(sketch, "E79.2", {"start": v(90, 70) * mm, "mid": v(87.07, 77.07) * mm, "end": v(80, 80) * mm});
            skLineSegment(sketch, "E79.3", {"start": v(90, -70) * mm, "end": v(90, 70) * mm});
            skArc(sketch, "E79.4", {"start": v(80, -80) * mm, "mid": v(87.07, -77.07) * mm, "end": v(90, -70) * mm});
            skLineSegment(sketch, "E79.5", {"start": v(-80, -80) * mm, "end": v(80, -80) * mm});
            skArc(sketch, "E79.6", {"start": v(-90, -70) * mm, "mid": v(-87.07, -77.07) * mm, "end": v(-80, -80) * mm});
            skLineSegment(sketch, "E79.7", {"start": v(-90, -70) * mm, "end": v(-90, 70) * mm});
            skCircle(sketch, "E79.8", {"center": v(-60, -53.33) * mm, "radius": 4 * mm});
            skCircle(sketch, "E79.9", {"center": v(60, -53.33) * mm, "radius": 4 * mm});
            skCircle(sketch, "E79.10", {"center": v(60, 53.33) * mm, "radius": 4 * mm});
            skCircle(sketch, "E79.11", {"center": v(-60, 53.33) * mm, "radius": 4 * mm});
            skArc(sketch, "E79.12", {"start": v(52.38, 47.01) * mm, "mid": v(0, 53.33) * mm, "end": v(-52.38, 47.01) * mm});
            skArc(sketch, "E79.13", {"start": v(-52.38, 47.01) * mm, "mid": v(-57.87, 43.47) * mm, "end": v(-60, 37.3) * mm});
            skLineSegment(sketch, "E79.14", {"start": v(-60, 37.3) * mm, "end": v(-60, -37.3) * mm});
            skArc(sketch, "E79.15", {"start": v(-60, -37.3) * mm, "mid": v(-57.87, -43.47) * mm, "end": v(-52.38, -47.01) * mm});
            skArc(sketch, "E79.16", {"start": v(-52.38, -47.01) * mm, "mid": v(0, -53.33) * mm, "end": v(52.38, -47.01) * mm});
            skArc(sketch, "E79.17", {"start": v(52.38, -47.01) * mm, "mid": v(57.87, -43.47) * mm, "end": v(60, -37.3) * mm});
            skLineSegment(sketch, "E79.18", {"start": v(60, 37.3) * mm, "end": v(60, -37.3) * mm});
            skArc(sketch, "E79.19", {"start": v(60, 37.3) * mm, "mid": v(57.87, 43.47) * mm, "end": v(52.38, 47.01) * mm});
            skLineSegment(sketch, "E80", {"start": v(0, 80) * mm, "end": v(0, 110) * mm});
            skPoint(sketch, "E80.endSnap0", {"position": v(0, 80) * mm});
            skCircle(sketch, "E81", {"center": v(0, 110) * mm, "radius": 6 * mm});
            skLineSegment(sketch, "E82", {"start": v(-33, 80) * mm, "end": v(-15, 98) * mm});
            skLineSegment(sketch, "E83", {"start": v(-15, 98) * mm, "end": v(-15, 110) * mm});
            skLineSegment(sketch, "E84", {"start": v(33, 80) * mm, "end": v(15, 98) * mm});
            skLineSegment(sketch, "E85", {"start": v(15, 98) * mm, "end": v(15, 110) * mm});
            skArc(sketch, "E86", {"start": v(15, 110) * mm, "mid": v(0, 125) * mm, "end": v(-15, 110) * mm});
            skPoint(sketch, "E87.endSnap0", {"position": v(0, -80) * mm});
            skLineSegment(sketch, "E88", {"start": v(-90, 0) * mm, "end": v(90, 0) * mm, "construction": true});
            skLineSegment(sketch, "E89.MirrorCS", {"start": v(-33, -80) * mm, "end": v(-15, -98) * mm});
            skLineSegment(sketch, "E90.MirrorCS", {"start": v(-15, -98) * mm, "end": v(-15, -110) * mm});
            skArc(sketch, "E91.MirrorCS", {"start": v(15, -110) * mm, "mid": v(0, -125) * mm, "end": v(-15, -110) * mm});
            skLineSegment(sketch, "E92.MirrorCS", {"start": v(15, -98) * mm, "end": v(15, -110) * mm});
            skLineSegment(sketch, "E93.MirrorCS", {"start": v(33, -80) * mm, "end": v(15, -98) * mm});
            skCircle(sketch, "E94.MirrorC", {"center": v(0, -110) * mm, "radius": 6 * mm});
            skLineSegment(sketch, "E95.MirrorCS", {"start": v(0, -80) * mm, "end": v(0, -110) * mm});
            skSolve(sketch);
        }
        {
            var Q0;
            Q0=makeQuery(id+"F16.imprint","IMPRINT",FACE,{"disambiguationData":[TD([[makeQuery(id+"F16.imprint","IMPRINT",EDGE,{"derivedFrom":sQuery(id+"F16.wireOp",EDGE,"E81")}),-1.0]])]});
            var Q1;
            {var subQ0=sQuery(id+"F16.wireOp",EDGE,"E89.MirrorCS");Q1=makeQuery(id+"F16.imprint","IMPRINT",FACE,{"disambiguationData":[TD([[makeQuery(id+"F16.imprint","IMPRINT",EDGE,{"derivedFrom":subQ0}),1.0]])]});}
            var Q2;
            Q2=makeQuery(id+"F2.opExtrude","CAP_FACE",FACE,{"disambiguationData":[OSD([sQuery(id+"F0.wireOp",EDGE,"E12"),sQuery(id+"F0.wireOp",EDGE,"E13"),sQuery(id+"F0.wireOp",EDGE,"E14"),sQuery(id+"F0.wireOp",EDGE,"E15"),sQuery(id+"F0.wireOp",EDGE,"E17.filletArc"),sQuery(id+"F0.wireOp",EDGE,"E18.filletArc"),sQuery(id+"F0.wireOp",EDGE,"E19.filletArc"),sQuery(id+"F0.wireOp",EDGE,"E20.filletArc"),sQuery(id+"F0.wireOp",EDGE,"E25.0"),sQuery(id+"F0.wireOp",EDGE,"E25.1"),sQuery(id+"F0.wireOp",EDGE,"E25.2"),sQuery(id+"F0.wireOp",EDGE,"E25.3"),sQuery(id+"F0.wireOp",EDGE,"E25.4"),sQuery(id+"F0.wireOp",EDGE,"E25.5"),sQuery(id+"F0.wireOp",EDGE,"E25.6"),sQuery(id+"F0.wireOp",EDGE,"E25.7")])],"isStart":false});
            extrude(context, id + "F17", {"entities" : qUnion([Q0, Q1]), "endBound" : BoundingType.UP_TO_SURFACE, "endBoundEntityFace" : qUnion([Q2]), "depth" : 4.5 * mm});
        }
        {
            var Q0;
            {var subQ11=sQuery(id+"F16.wireOp",EDGE,"E79.0");Q0=makeQuery(id+"F16.imprint","IMPRINT",FACE,{"disambiguationData":[TD([[makeQuery(id+"F16.imprint","IMPRINT",EDGE,{"derivedFrom":subQ11}),1.0]])]});}
            var Q1;
            Q1=makeQuery(id+"F2.opExtrude","CAP_FACE",FACE,{"disambiguationData":[OSD([sQuery(id+"F0.wireOp",EDGE,"E12"),sQuery(id+"F0.wireOp",EDGE,"E13"),sQuery(id+"F0.wireOp",EDGE,"E14"),sQuery(id+"F0.wireOp",EDGE,"E15"),sQuery(id+"F0.wireOp",EDGE,"E17.filletArc"),sQuery(id+"F0.wireOp",EDGE,"E18.filletArc"),sQuery(id+"F0.wireOp",EDGE,"E19.filletArc"),sQuery(id+"F0.wireOp",EDGE,"E20.filletArc"),sQuery(id+"F0.wireOp",EDGE,"E25.0"),sQuery(id+"F0.wireOp",EDGE,"E25.1"),sQuery(id+"F0.wireOp",EDGE,"E25.2"),sQuery(id+"F0.wireOp",EDGE,"E25.3"),sQuery(id+"F0.wireOp",EDGE,"E25.4"),sQuery(id+"F0.wireOp",EDGE,"E25.5"),sQuery(id+"F0.wireOp",EDGE,"E25.6"),sQuery(id+"F0.wireOp",EDGE,"E25.7")])],"isStart":false});
            extrude(context, id + "F18", {"entities" : qUnion([Q0]), "endBound" : BoundingType.UP_TO_SURFACE, "endBoundEntityFace" : qUnion([Q1]), "depth" : 4.6 * mm});
        }
    });
